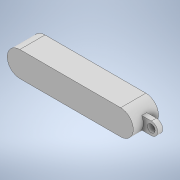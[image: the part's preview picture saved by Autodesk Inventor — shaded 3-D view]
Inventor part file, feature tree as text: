
AUTODESK INVENTOR PART (.ipt)
format: ipt  version: 2022 (Build 260153000, 153)  size: 123,904 bytes
history: native  units: mm
features: extrude x2, sketch x2, plane x1, projected_geometry x1
ambient origin geometry x8: Origin, YZ Plane, XZ Plane, XY Plane, X Axis, Y Axis, Z Axis, Center Point
bodies: Solid1 (feature_tree)
feature tree (6):
  extrude  "Extrusion1"  Depth=20.0mm
  plane  "Work Plane1"
  extrude  "Extrusion2"  Depth=20.0mm
  sketch  "Sketch1"  dims[d0=20.0mm d3=6.0mm]
  sketch  "Sketch2"  dims[d5=6.0mm d6=20.0mm d7=0.0mm d8=10.0mm d9=6.0mm d10=4.0mm d11=0.0mm d16=30.0mm d17=30.0mm d18=80.0mm]
  projected_geometry  "Projected Loop1"
